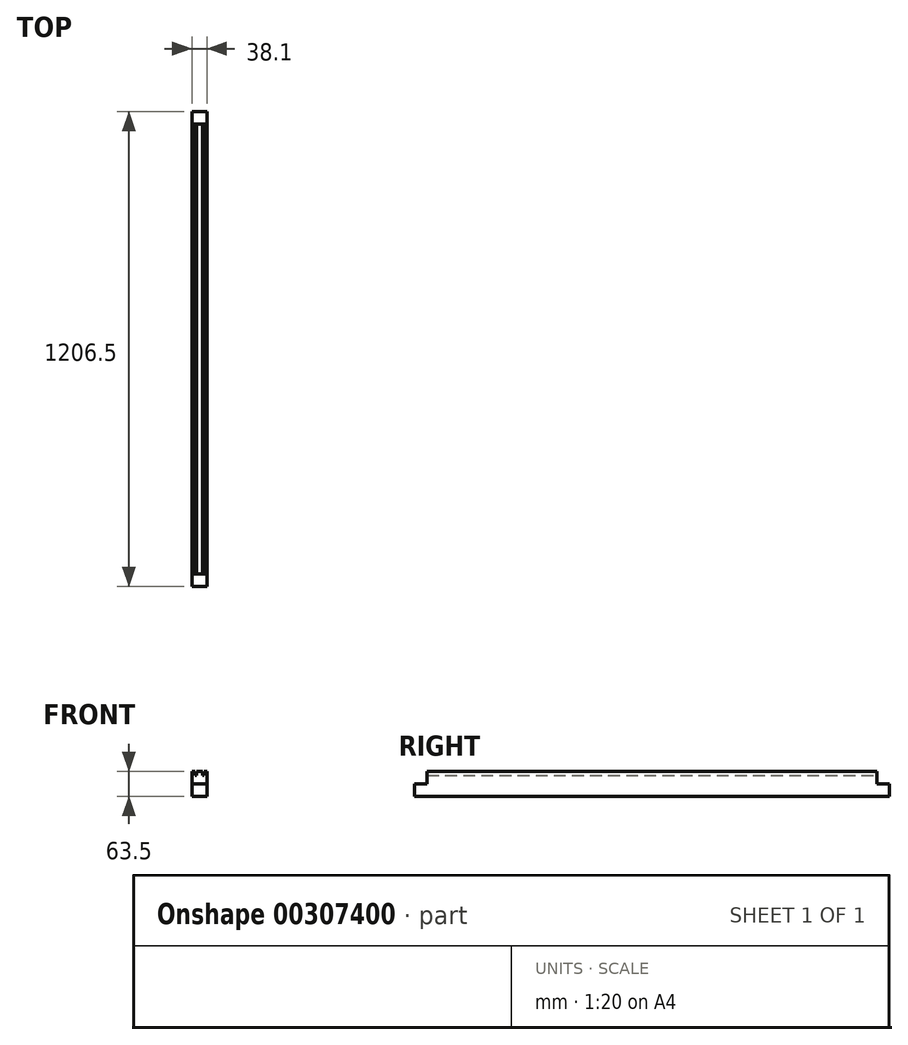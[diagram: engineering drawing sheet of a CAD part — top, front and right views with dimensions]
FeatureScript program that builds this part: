
annotation { "Feature Type Name" : "Feature", "Feature Type Description" : "" }
export const myFeature = defineFeature(function(context is Context, id is Id, definition is map)
    precondition{}
    {
        {
            var Q0;
            Q0=qCreatedBy(makeId("Front.planeOp"),FACE);
            var sketch = newSketch(context, id + "F0", { "sketchPlane" : qUnion([Q0])});
            skLineSegment(sketch, "E0.bottom", {"start": v(19.05, -31.75) * mm, "end": v(-19.05, -31.75) * mm});
            skLineSegment(sketch, "E0.top", {"start": v(19.05, 31.75) * mm, "end": v(-19.05, 31.75) * mm});
            skLineSegment(sketch, "E0.left", {"start": v(19.05, -31.75) * mm, "end": v(19.05, 31.75) * mm});
            skLineSegment(sketch, "E0.right", {"start": v(-19.05, -31.75) * mm, "end": v(-19.05, 31.75) * mm});
            skPoint(sketch, "E0.middle", {"position": v(0, 0) * mm});
            skLineSegment(sketch, "E1.bottom", {"start": v(11.11, 21.59) * mm, "end": v(7.94, 21.59) * mm});
            skLineSegment(sketch, "E1.top", {"start": v(11.11, 31.75) * mm, "end": v(7.94, 31.75) * mm});
            skLineSegment(sketch, "E1.left", {"start": v(11.11, 21.59) * mm, "end": v(11.11, 31.75) * mm});
            skLineSegment(sketch, "E1.right", {"start": v(7.94, 21.59) * mm, "end": v(7.94, 31.75) * mm});
            skPoint(sketch, "E1.middle", {"position": v(9.53, 26.67) * mm});
            skLineSegment(sketch, "E2.bottom", {"start": v(-7.94, 21.59) * mm, "end": v(-11.11, 21.59) * mm});
            skLineSegment(sketch, "E2.top", {"start": v(-7.94, 31.75) * mm, "end": v(-11.11, 31.75) * mm});
            skLineSegment(sketch, "E2.left", {"start": v(-7.94, 21.59) * mm, "end": v(-7.94, 31.75) * mm});
            skLineSegment(sketch, "E2.right", {"start": v(-11.11, 21.59) * mm, "end": v(-11.11, 31.75) * mm});
            skPoint(sketch, "E2.middle", {"position": v(-9.53, 26.67) * mm});
            skSolve(sketch);
        }
        {
            var Q0;
            Q0=makeQuery(id+"F0.imprint","IMPRINT",FACE,{"disambiguationData":[TD([[makeQuery(id+"F0.imprint","IMPRINT",EDGE,{"derivedFrom":sQuery(id+"F0.wireOp",EDGE,"E0.bottom")}),-1.0]])]});
            extrude(context, id + "F1", {"entities" : qUnion([Q0]), "endBound" : BoundingType.SYMMETRIC, "depth" : 1206.5 * mm});
        }
        {
            var Q0;
            Q0=makeQuery(id+"F1.opExtrude","SWEPT_FACE",FACE,{"disambiguationData":[OSD([sQuery(id+"F0.wireOp",EDGE,"E0.right")])]});
            var sketch = newSketch(context, id + "F2", { "sketchPlane" : qUnion([Q0])});
            skLineSegment(sketch, "E3", {"start": v(0, 31.75) * mm, "end": v(0, -31.75) * mm, "construction": true});
            skPoint(sketch, "E3.endSnap0", {"position": v(0, -31.75) * mm});
            skLineSegment(sketch, "E4.bottom", {"start": v(603.25, 31.75) * mm, "end": v(571.5, 31.75) * mm});
            skLineSegment(sketch, "E4.top", {"start": v(603.25, 0) * mm, "end": v(571.5, 0) * mm});
            skLineSegment(sketch, "E4.left", {"start": v(603.25, 31.75) * mm, "end": v(603.25, 0) * mm});
            skLineSegment(sketch, "E4.right", {"start": v(571.5, 31.75) * mm, "end": v(571.5, 0) * mm});
            skLineSegment(sketch, "E5.MirrorCS", {"start": v(-603.25, 31.75) * mm, "end": v(-571.5, 31.75) * mm});
            skLineSegment(sketch, "E6.MirrorCS", {"start": v(-603.25, 0) * mm, "end": v(-571.5, 0) * mm});
            skLineSegment(sketch, "E7.MirrorCS", {"start": v(-603.25, 31.75) * mm, "end": v(-603.25, 0) * mm});
            skLineSegment(sketch, "E8.MirrorCS", {"start": v(-571.5, 31.75) * mm, "end": v(-571.5, 0) * mm});
            skSolve(sketch);
        }
        {
            var Q0;
            Q0 = qSketchRegion(id + "F2", true);
            extrude(context, id + "F3", {"entities" : qUnion([Q0]), "operationType" : NewBodyOperationType.REMOVE, "endBound" : BoundingType.THROUGH_ALL, "oppositeDirection" : true, "depth" : 25.4 * mm});
        }
    });
